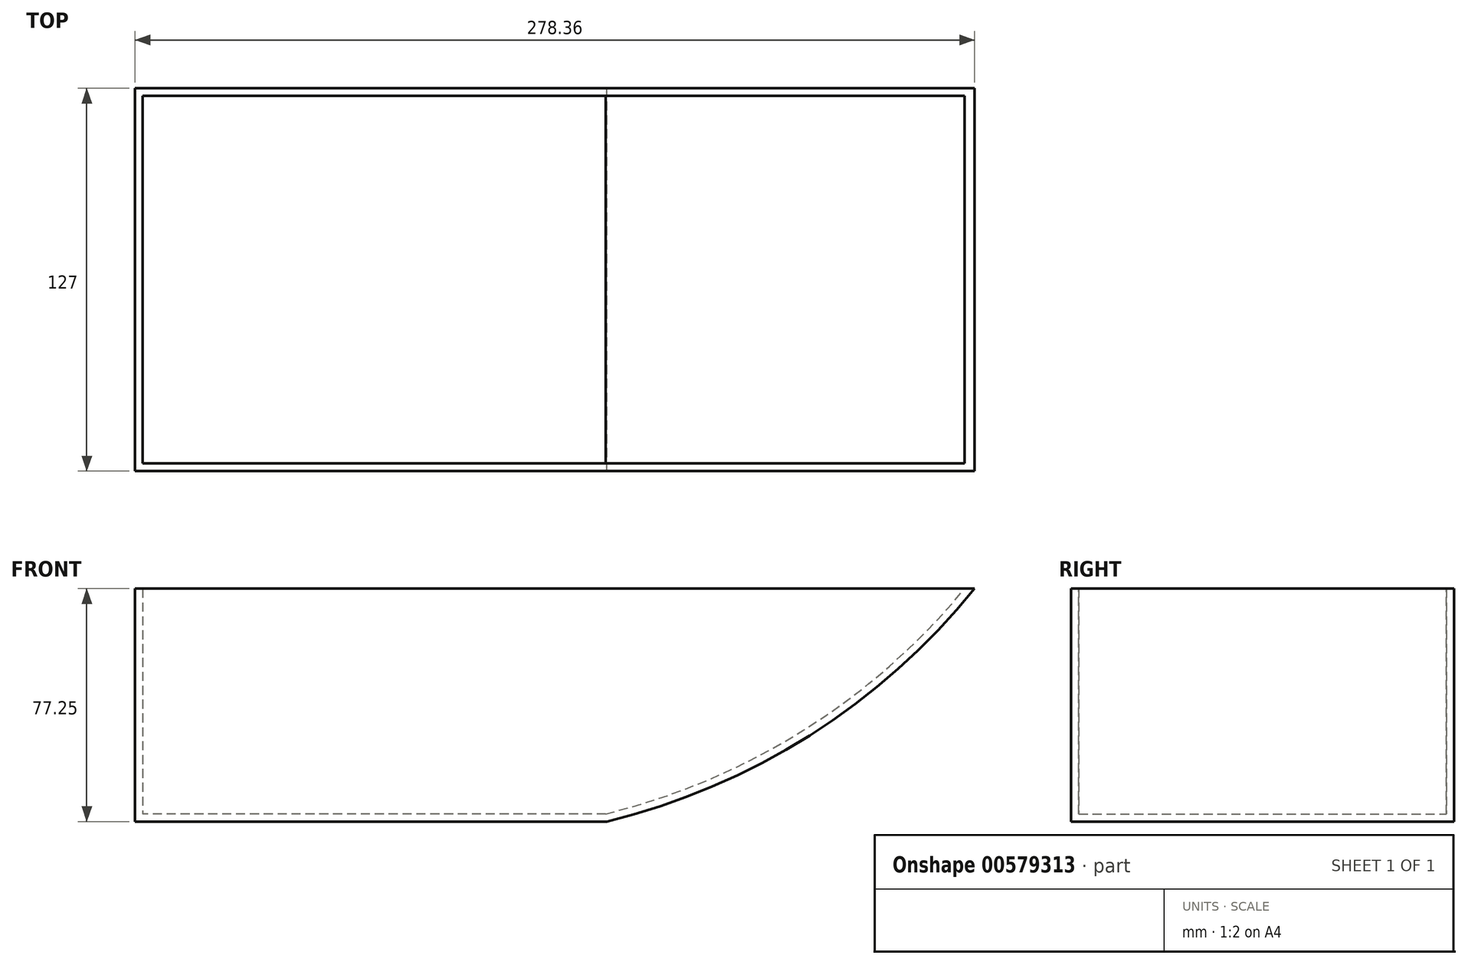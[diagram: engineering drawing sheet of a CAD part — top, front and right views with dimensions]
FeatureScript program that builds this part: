
annotation { "Feature Type Name" : "Feature", "Feature Type Description" : "" }
export const myFeature = defineFeature(function(context is Context, id is Id, definition is map)
    precondition{}
    {
        {
            var Q0;
            Q0=qCreatedBy(makeId("Front.planeOp"),FACE);
            var sketch = newSketch(context, id + "F0", { "sketchPlane" : qUnion([Q0])});
            skLineSegment(sketch, "E0", {"start": v(0, 0) * mm, "end": v(-156.37, 0) * mm});
            skLineSegment(sketch, "E1", {"start": v(-156.37, 0) * mm, "end": v(-156.37, -77.25) * mm});
            skLineSegment(sketch, "E2", {"start": v(0, 0) * mm, "end": v(121.99, 0) * mm});
            skArc(sketch, "E3", {"start": v(0, -77.25) * mm, "mid": v(67.36, -48.68) * mm, "end": v(121.99, 0) * mm});
            skLineSegment(sketch, "E4", {"start": v(0, -77.25) * mm, "end": v(-156.37, -77.25) * mm});
            skLineSegment(sketch, "E5", {"start": v(0, 0) * mm, "end": v(0, 0) * mm});
            skSolve(sketch);
        }
        {
            var Q0;
            Q0=makeQuery(id+"F0.imprint","IMPRINT",FACE,{"disambiguationData":[TD([[makeQuery(id+"F0.imprint","IMPRINT",EDGE,{"derivedFrom":sQuery(id+"F0.wireOp",EDGE,"E0")}),1.0]])]});
            extrude(context, id + "F1", {"entities" : qUnion([Q0]), "depth" : 127 * mm, "offsetDistance" : 25.4 * mm});
        }
        {
            var Q0;
            Q0=makeQuery(id+"F1.opExtrude","SWEPT_FACE",FACE,{"disambiguationData":[OSD([sQuery(id+"F0.wireOp",EDGE,"E0"),sQuery(id+"F0.wireOp",EDGE,"E2")])]});
            shell(context, id + "F2", {"entities" : qUnion([Q0]), "thickness" : 2.54 * mm});
        }
    });
